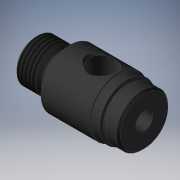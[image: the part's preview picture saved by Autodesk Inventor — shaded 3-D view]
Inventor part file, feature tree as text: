
AUTODESK INVENTOR PART (.ipt)
format: ipt  version: 2019 (Build 230136000, 136)  size: 247,296 bytes
history: native  units: mm
features: other x91, sketch x6, revolve x5, thread x1, extrude x1
ambient origin geometry x8: Origin, YZ Plane, XZ Plane, XY Plane, X Axis, Y Axis, Z Axis, Center Point
bodies: Solid1 (feature_tree)
feature tree (104):
  revolve  "Revolution1"  Angle=360.0deg
  revolve  "Revolution2"  Angle=360.0deg
  thread  "Thread1"  [1 undecoded]
  revolve  "Revolution3"  Angle=360.0deg
  extrude  "Extrusion1"  [1 undecoded]
  revolve  "Revolution4"  [1 undecoded]
  revolve  "Revolution5"  [1 undecoded]
  other  "b1_XY"
  other  "b1_YZ"
  other  "b1_ZX"
  other  "b1_X"
  other  "b1_Y"
  other  "b1_Z"
  other  "b1_Center"
  other  "b2_XY"
  other  "b2_YZ"
  other  "b2_ZX"
  other  "b2_X"
  other  "b2_Y"
  other  "b2_Z"
  other  "b2_Center"
  other  "cl1_XY"
  other  "cl1_YZ"
  other  "cl1_ZX"
  other  "cl1_X"
  other  "cl1_Y"
  other  "cl1_Z"
  other  "cl1_Center"
  other  "cl2_XY"
  other  "cl2_YZ"
  other  "cl2_ZX"
  other  "cl2_X"
  other  "cl2_Y"
  other  "cl2_Z"
  other  "cl2_Center"
  other  "ee_XY"
  other  "ee_YZ"
  other  "ee_ZX"
  other  "ee_X"
  other  "ee_Y"
  other  "ee_Z"
  other  "ee_Center"
  other  "od1_XY"
  other  "od1_YZ"
  other  "od1_ZX"
  other  "od1_X"
  other  "od1_Y"
  other  "od1_Z"
  other  "od1_Center"
  other  "od2_XY"
  other  "od2_YZ"
  other  "od2_ZX"
  other  "od2_X"
  other  "od2_Y"
  other  "od2_Z"
  other  "od2_Center"
  other  "od3_XY"
  other  "od3_YZ"
  other  "od3_ZX"
  other  "od3_X"
  other  "od3_Y"
  other  "od3_Z"
  other  "od3_Center"
  other  "od4_XY"
  other  "od4_YZ"
  other  "od4_ZX"
  other  "od4_X"
  other  "od4_Y"
  other  "od4_Z"
  other  "od4_Center"
  other  "to_body_XY"
  other  "to_body_YZ"
  other  "to_body_ZX"
  other  "to_body_X"
  other  "to_body_Y"
  other  "to_body_Z"
  other  "to_body_Center"
  other  "to_dummy_XY"
  other  "to_dummy_YZ"
  other  "to_dummy_ZX"
  other  "to_dummy_X"
  other  "to_dummy_Y"
  other  "to_dummy_Z"
  other  "to_dummy_Center"
  other  "to_nut_XY"
  other  "to_nut_YZ"
  other  "to_nut_ZX"
  other  "to_nut_X"
  other  "to_nut_Y"
  other  "to_nut_Z"
  other  "to_nut_Center"
  other  "to_stroke_adjuster_XY"
  other  "to_stroke_adjuster_YZ"
  other  "to_stroke_adjuster_ZX"
  other  "to_stroke_adjuster_X"
  other  "to_stroke_adjuster_Y"
  other  "to_stroke_adjuster_Z"
  other  "to_stroke_adjuster_Center"
  sketch  "Sketch_1"  dims[d0=360.0deg d1=360.0deg]
  sketch  "Sketch_2"  dims[d2=7.28853mm d3=0.0mm d4=360.0deg d5=111.0488mm d6=0.0mm]
  sketch  "Sketch_6"  dims[d7=360.0deg d8=360.0deg]
  sketch  "Sketch_7"  dims[d9=0.0mm d10=0.0mm d11=0.0mm d12=0.0mm d13=0.0mm d14=0.0mm d15=0.0mm d16=0.0mm d17=0.0mm d18=0.0mm]
  sketch  "Sketch_8"
  sketch  "Sketch_29"
note: 4 required parameter values undecoded (feature->parameter linkage not recoverable at this tier; creation-order binding heuristic only, values carry confidence <= 0.55)
